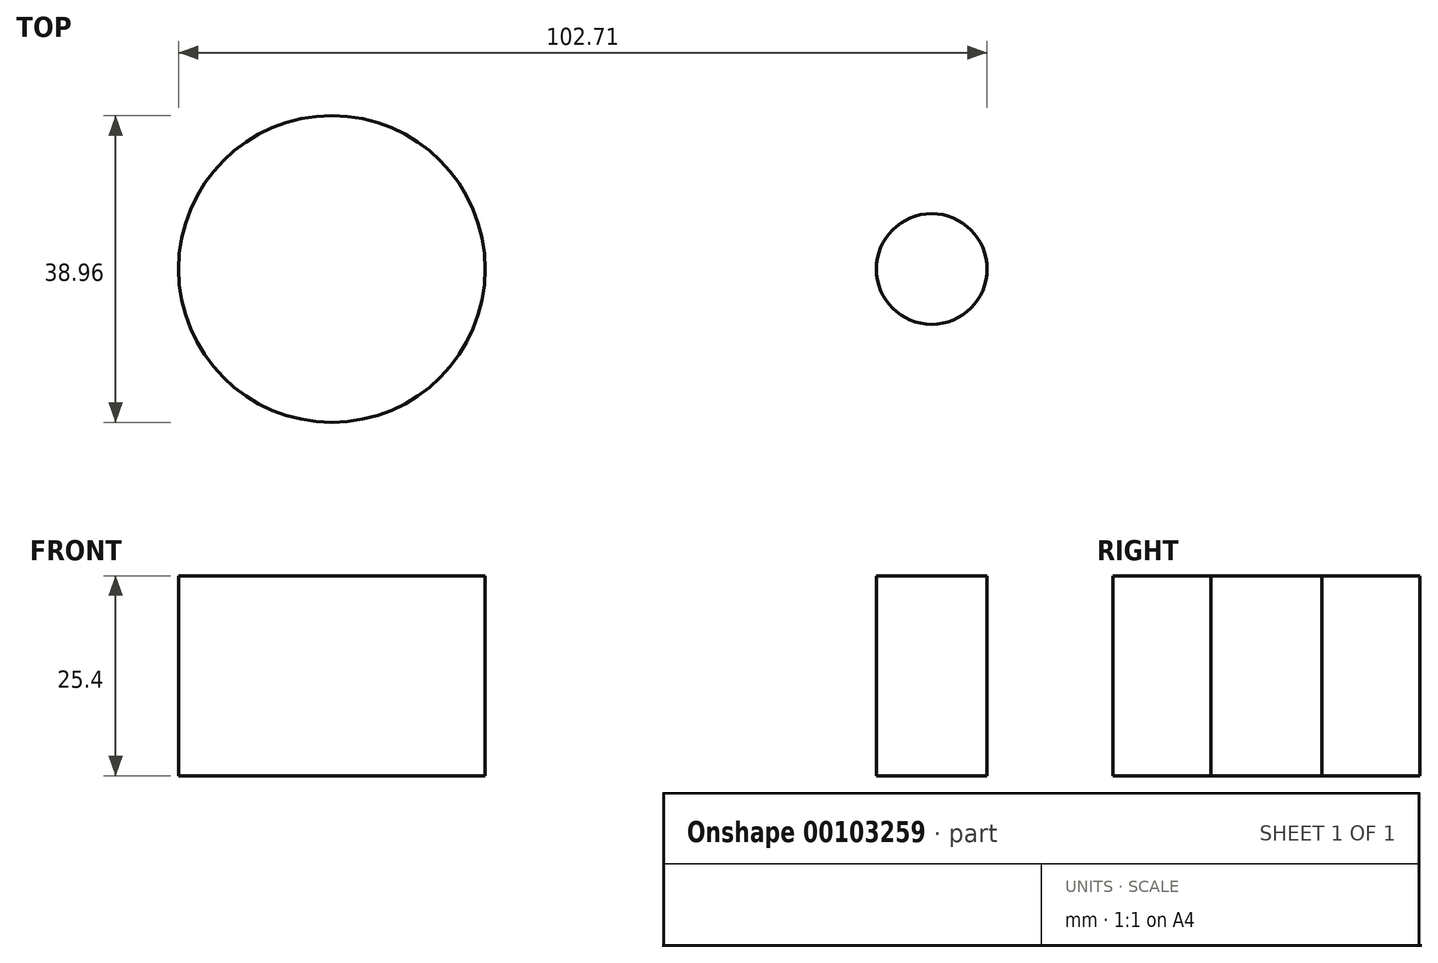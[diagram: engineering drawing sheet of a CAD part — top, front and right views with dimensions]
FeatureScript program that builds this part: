
annotation { "Feature Type Name" : "Feature", "Feature Type Description" : "" }
export const myFeature = defineFeature(function(context is Context, id is Id, definition is map)
    precondition{}
    {
        {
            var Q0;
            Q0=qCreatedBy(makeId("Top.planeOp"),FACE);
            var sketch = newSketch(context, id + "F0", { "sketchPlane" : qUnion([Q0])});
            skLineSegment(sketch, "E0.bottom", {"start": v(0, 0) * mm, "end": v(76.2, 0) * mm});
            skLineSegment(sketch, "E0.top", {"start": v(0, -50.8) * mm, "end": v(76.2, -50.8) * mm});
            skLineSegment(sketch, "E0.left", {"start": v(0, 0) * mm, "end": v(0, -50.8) * mm});
            skLineSegment(sketch, "E0.right", {"start": v(76.2, 0) * mm, "end": v(76.2, -50.8) * mm});
            skCircle(sketch, "E1", {"center": v(0, 0) * mm, "radius": 11.43 * mm});
            skSolve(sketch);
        }
        {
            var Q0;
            Q0=qCreatedBy(makeId("Top.planeOp"),FACE);
            var sketch = newSketch(context, id + "F1", { "sketchPlane" : qUnion([Q0])});
            skCircle(sketch, "E2", {"center": v(0, -50.8) * mm, "radius": 19.48 * mm});
            skCircle(sketch, "E3", {"center": v(76.2, -50.8) * mm, "radius": 7.03 * mm});
            skSolve(sketch);
        }
        {
            var Q0;
            {var subQ0=sQuery(id+"F1.wireOp",EDGE,"E3");var subQ1=sQuery(id+"F1.wireOp",EDGE,"E2");var subQ2=makeQuery(id+"F1.imprint","INTERSECT",VERTEX,{"disambiguationData":[OD(0.0)],"derivedFrom":[subQ1,subQ0]});Q0=makeQuery(id+"F1.imprint","IMPRINT",FACE,{"disambiguationData":[TD([[makeQuery(id+"F1.imprint","IMPRINT",EDGE,{"disambiguationData":[TD([[subQ2,1.0]])],"derivedFrom":subQ1}),1.0]])]});}
            var Q1;
            {var subQ0=sQuery(id+"F1.wireOp",EDGE,"E3");var subQ1=sQuery(id+"F1.wireOp",EDGE,"E2");var subQ2=makeQuery(id+"F1.imprint","INTERSECT",VERTEX,{"disambiguationData":[OD(0.0)],"derivedFrom":[subQ1,subQ0]});Q1=makeQuery(id+"F1.imprint","IMPRINT",FACE,{"disambiguationData":[TD([[makeQuery(id+"F1.imprint","IMPRINT",EDGE,{"disambiguationData":[TD([[subQ2,-1.0]])],"derivedFrom":subQ1}),-1.0]])]});}
            var Q2;
            Q2=makeQuery(id+"F1.imprint","IMPRINT",FACE,{"disambiguationData":[TD([[makeQuery(id+"F1.imprint","IMPRINT",EDGE,{"derivedFrom":sQuery(id+"F1.wireOp",EDGE,"E2")}),1.0]])]});
            var Q3;
            Q3=makeQuery(id+"F1.imprint","IMPRINT",FACE,{"disambiguationData":[TD([[makeQuery(id+"F1.imprint","IMPRINT",EDGE,{"derivedFrom":sQuery(id+"F1.wireOp",EDGE,"E3")}),1.0]])]});
            extrude(context, id + "F2", {"entities" : qUnion([Q0, Q1, Q2, Q3]), "depth" : 25.4 * mm});
        }
    });
